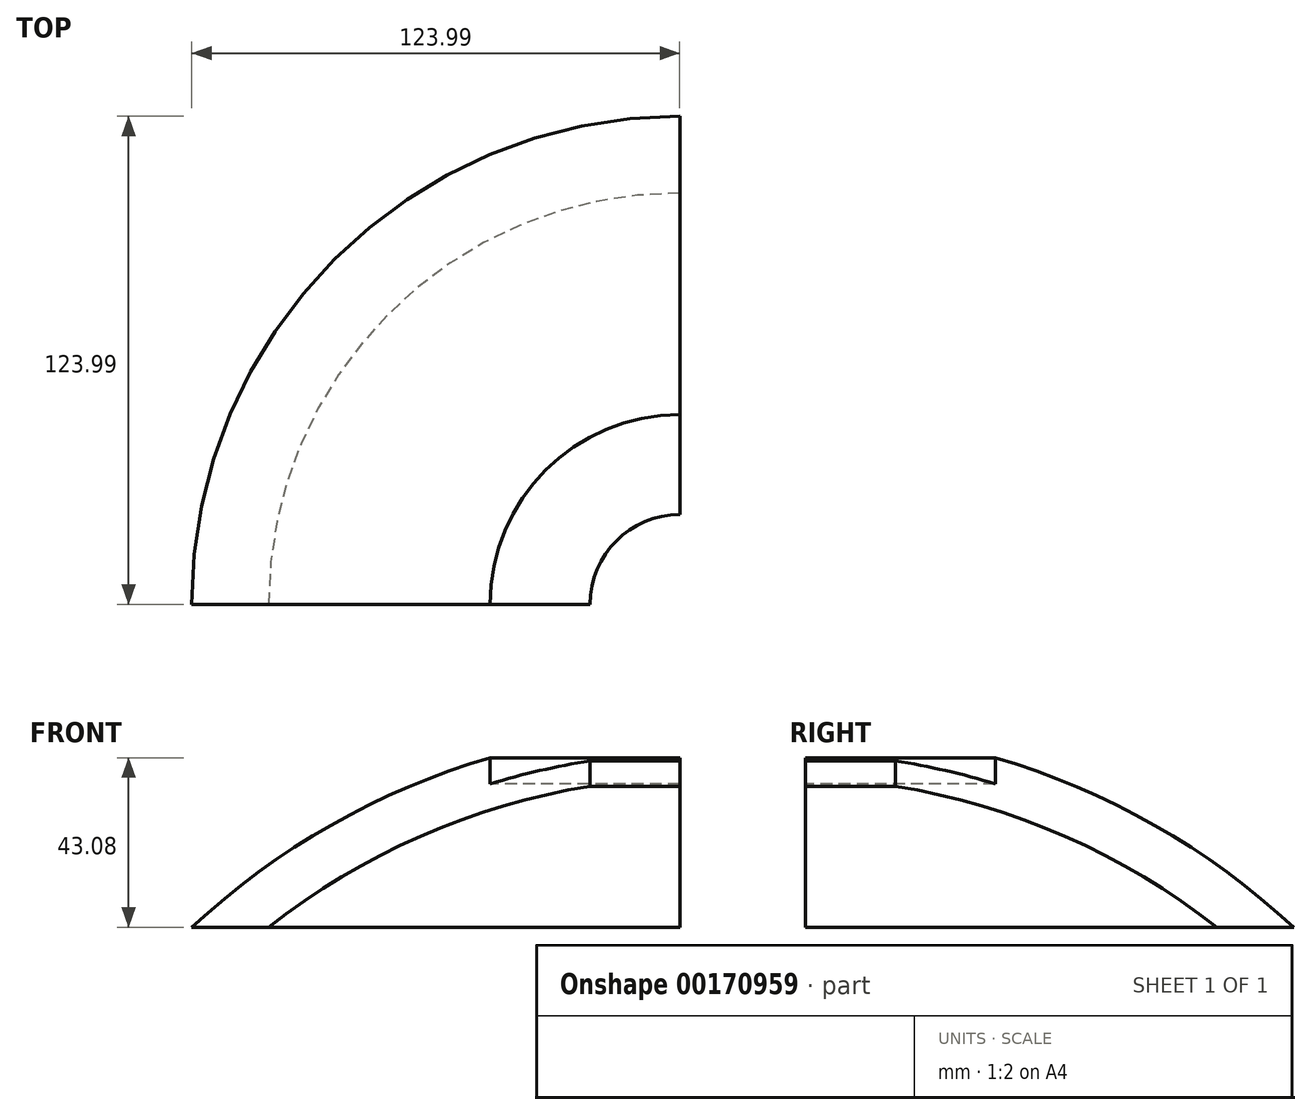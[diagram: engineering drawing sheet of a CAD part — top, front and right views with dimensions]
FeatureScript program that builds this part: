
annotation { "Feature Type Name" : "Feature", "Feature Type Description" : "" }
export const myFeature = defineFeature(function(context is Context, id is Id, definition is map)
    precondition{}
    {
        {
            var Q0;
            Q0=qCreatedBy(makeId("Front.planeOp"),FACE);
            var sketch = newSketch(context, id + "F0", { "sketchPlane" : qUnion([Q0])});
            skLineSegment(sketch, "E0", {"start": v(-5.53, 152.4) * mm, "end": v(-114.3, 152.4) * mm});
            skLineSegment(sketch, "E1", {"start": v(-129.52, 139.7) * mm, "end": v(-119.98, 139.7) * mm});
            skArc(sketch, "E2.trimOffspring", {"start": v(-28.29, 175.54) * mm, "mid": v(-61.04, 167) * mm, "end": v(-91.58, 152.4) * mm});
            skArc(sketch, "E3.trimOffspring", {"start": v(-28.29, 181.96) * mm, "mid": v(-67.47, 171.35) * mm, "end": v(-103.37, 152.4) * mm});
            skArc(sketch, "E4.trimOffspring", {"start": v(-53.69, 182.78) * mm, "mid": v(-85.36, 170.3) * mm, "end": v(-114.3, 152.4) * mm});
            skArc(sketch, "E5", {"start": v(-114.3, 152.4) * mm, "mid": v(-122.07, 146.25) * mm, "end": v(-129.52, 139.7) * mm});
            skLineSegment(sketch, "E6", {"start": v(-28.29, 181.96) * mm, "end": v(-28.29, 175.54) * mm});
            skLineSegment(sketch, "E7", {"start": v(-53.69, 182.78) * mm, "end": v(-53.69, 176.15) * mm});
            skLineSegment(sketch, "E8", {"start": v(-5.53, 191.17) * mm, "end": v(-5.53, 152.4) * mm});
            skLineSegment(sketch, "E9", {"start": v(-119.98, 139.7) * mm, "end": v(-109.99, 139.7) * mm});
            skArc(sketch, "E10", {"start": v(-28.29, 161.99) * mm, "mid": v(-45.28, 158.08) * mm, "end": v(-61.76, 152.4) * mm});
            skArc(sketch, "E11", {"start": v(-91.58, 152.4) * mm, "mid": v(-100.98, 146.34) * mm, "end": v(-109.99, 139.7) * mm});
            skLineSegment(sketch, "E12", {"start": v(-28.29, 175.54) * mm, "end": v(-28.29, 161.99) * mm});
            skSolve(sketch);
        }
        {
            var Q0;
            {var subQ4=sQuery(id+"F0.wireOp",EDGE,"E1");Q0=makeQuery(id+"F0.imprint","IMPRINT",FACE,{"disambiguationData":[TD([[makeQuery(id+"F0.imprint","IMPRINT",EDGE,{"derivedFrom":subQ4}),1.0]])]});}
            var Q1;
            {var subQ0=sQuery(id+"F0.wireOp",EDGE,"E4.trimOffspring");Q1=makeQuery(id+"F0.imprint","IMPRINT",FACE,{"disambiguationData":[TD([[makeQuery(id+"F0.imprint","IMPRINT",EDGE,{"derivedFrom":subQ0}),1.0]])]});}
            var Q2;
            {var subQ0=sQuery(id+"F0.wireOp",EDGE,"E2.trimOffspring");Q2=makeQuery(id+"F0.imprint","IMPRINT",FACE,{"disambiguationData":[TD([[makeQuery(id+"F0.imprint","IMPRINT",EDGE,{"derivedFrom":subQ0}),-1.0]])]});}
            var Q3;
            Q3=sQuery(id+"F0.wireOp",EDGE,"E8");
            revolve(context, id + "F1", {"surfaceOperationType" : NewSurfaceOperationType.NEW, "entities" : qUnion([Q0, Q1, Q2]), "axis" : qUnion([Q3]), "revolveType" : RevolveType.ONE_DIRECTION, "angle" : 90 * degree});
        }
    });
